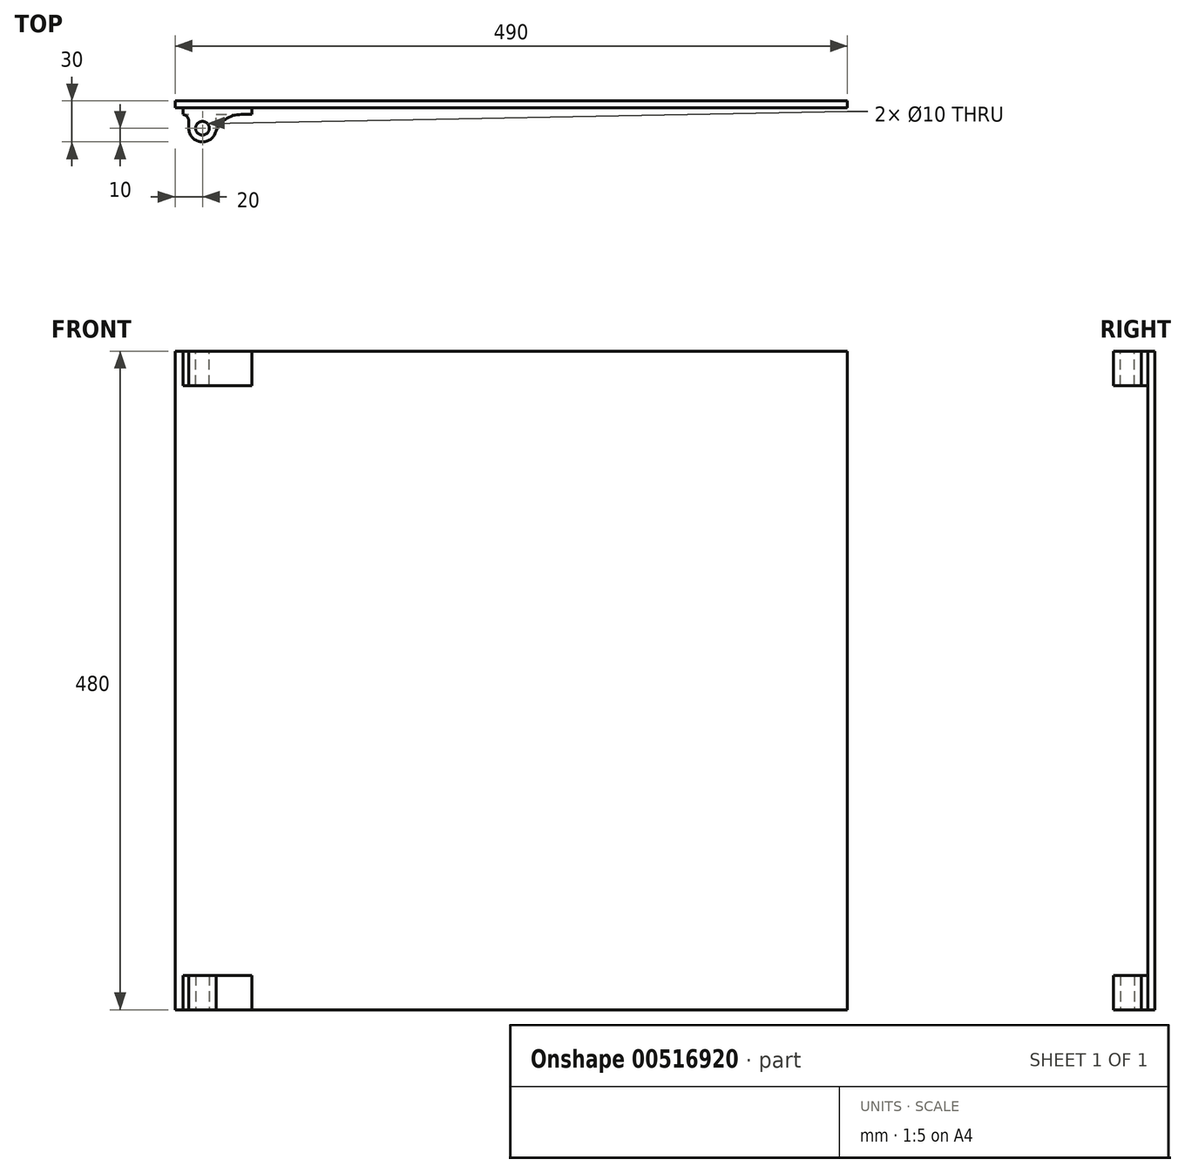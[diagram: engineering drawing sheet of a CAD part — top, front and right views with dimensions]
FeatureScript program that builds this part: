
annotation { "Feature Type Name" : "Feature", "Feature Type Description" : "" }
export const myFeature = defineFeature(function(context is Context, id is Id, definition is map)
    precondition{}
    {
        {
            var Q0;
            Q0=qCreatedBy(makeId("Front.planeOp"),FACE);
            var sketch = newSketch(context, id + "F0", { "sketchPlane" : qUnion([Q0])});
            skLineSegment(sketch, "E0.bottom", {"start": v(245, 240) * mm, "end": v(-245, 240) * mm});
            skLineSegment(sketch, "E0.top", {"start": v(245, -240) * mm, "end": v(-245, -240) * mm});
            skLineSegment(sketch, "E0.left", {"start": v(245, 240) * mm, "end": v(245, -240) * mm});
            skLineSegment(sketch, "E0.right", {"start": v(-245, 240) * mm, "end": v(-245, -240) * mm});
            skPoint(sketch, "E0.middle", {"position": v(0, 0) * mm});
            skSolve(sketch);
        }
        {
            var Q0;
            Q0=makeQuery(id+"F0.imprint","IMPRINT",FACE,{"disambiguationData":[TD([[makeQuery(id+"F0.imprint","IMPRINT",EDGE,{"derivedFrom":sQuery(id+"F0.wireOp",EDGE,"E0.bottom")}),1.0]])]});
            extrude(context, id + "F1", {"entities" : qUnion([Q0]), "depth" : 5 * mm, "offsetDistance" : 25 * mm});
        }
        {
            var Q0;
            Q0=makeQuery(id+"F1.opExtrude","SWEPT_FACE",FACE,{"disambiguationData":[OSD([sQuery(id+"F0.wireOp",EDGE,"E0.bottom")])]});
            var sketch = newSketch(context, id + "F2", { "sketchPlane" : qUnion([Q0])});
            skLineSegment(sketch, "E1.0", {"start": v(245, -5) * mm, "end": v(-245, -5) * mm});
            skLineSegment(sketch, "E2", {"start": v(-239, -5) * mm, "end": v(-239, -10) * mm});
            skLineSegment(sketch, "E3", {"start": v(-239, -10) * mm, "end": v(-189, -10) * mm});
            skLineSegment(sketch, "E4", {"start": v(-189, -10) * mm, "end": v(-189, -5) * mm});
            skLineSegment(sketch, "E5", {"start": v(-189, -5) * mm, "end": v(-239, -5) * mm});
            skCircle(sketch, "E6", {"center": v(-225, -20) * mm, "radius": 10 * mm});
            skCircle(sketch, "E7", {"center": v(-225, -20) * mm, "radius": 5 * mm});
            skLineSegment(sketch, "E8", {"start": v(-235, -20) * mm, "end": v(-235, -10) * mm});
            skLineSegment(sketch, "E9", {"start": v(-215, -20) * mm, "end": v(-215, -10) * mm});
            skSolve(sketch);
        }
        {
            var Q0;
            {var subQ4=sQuery(id+"F2.wireOp",EDGE,"E2");Q0=makeQuery(id+"F2.imprint","IMPRINT",FACE,{"disambiguationData":[TD([[makeQuery(id+"F2.imprint","IMPRINT",EDGE,{"derivedFrom":subQ4}),1.0]])]});}
            var Q1;
            Q1=makeQuery(id+"F2.imprint","IMPRINT",FACE,{"disambiguationData":[TD([[makeQuery(id+"F2.imprint","IMPRINT",EDGE,{"derivedFrom":sQuery(id+"F2.wireOp",EDGE,"E7")}),-1.0]])]});
            var Q2;
            {var subQ0=sQuery(id+"F2.wireOp",EDGE,"E9");Q2=makeQuery(id+"F2.imprint","IMPRINT",FACE,{"disambiguationData":[TD([[makeQuery(id+"F2.imprint","IMPRINT",EDGE,{"derivedFrom":subQ0}),1.0]])]});}
            var Q3;
            {var subQ0=sQuery(id+"F2.wireOp",EDGE,"E8");Q3=makeQuery(id+"F2.imprint","IMPRINT",FACE,{"disambiguationData":[TD([[makeQuery(id+"F2.imprint","IMPRINT",EDGE,{"derivedFrom":subQ0}),-1.0]])]});}
            extrude(context, id + "F3", {"entities" : qUnion([Q0, Q1, Q2, Q3]), "oppositeDirection" : true, "depth" : 25 * mm, "offsetDistance" : 25 * mm});
        }
        {
            var Q0;
            Q0=makeQuery(id+"F3.opExtrude","SWEPT_BODY",BODY,{"disambiguationData":[OSD([sQuery(id+"F2.wireOp",EDGE,"E2"),sQuery(id+"F2.wireOp",EDGE,"E3"),sQuery(id+"F2.wireOp",EDGE,"E4"),sQuery(id+"F2.wireOp",EDGE,"E5"),sQuery(id+"F2.wireOp",EDGE,"E6"),sQuery(id+"F2.wireOp",EDGE,"E7"),sQuery(id+"F2.wireOp",EDGE,"E8"),sQuery(id+"F2.wireOp",EDGE,"E9")])]});
            var Q1;
            Q1=qCreatedBy(makeId("Top.planeOp"),FACE);
            mirror(context, id + "F4", {"entities" : qUnion([Q0]), "mirrorPlane" : qUnion([Q1])});
        }
        {
            var Q0;
            Q0=makeQuery(id+"F1.opExtrude","CAP_FACE",FACE,{"disambiguationData":[OSD([sQuery(id+"F0.wireOp",EDGE,"E0.bottom"),sQuery(id+"F0.wireOp",EDGE,"E0.top"),sQuery(id+"F0.wireOp",EDGE,"E0.left"),sQuery(id+"F0.wireOp",EDGE,"E0.right")])],"isStart":false});
            var sketch = newSketch(context, id + "F5", { "sketchPlane" : qUnion([Q0])});
            skLineSegment(sketch, "E10", {"start": v(-239, -240) * mm, "end": v(-239, 240) * mm, "construction": true});
            skSolve(sketch);
        }
        {
            var Q0;
            Q0=makeQuery(id+"F3.opExtrude","SWEPT_EDGE",EDGE,{"disambiguationData":[OSD([sQuery(id+"F2.wireOp",EDGE,"E3"),sQuery(id+"F2.wireOp",EDGE,"E9")])]});
            fillet(context, id + "F6", {"entities" : qUnion([Q0]), "radius" : 20 * mm, "tangentPropagation" : true, "allowEdgeOverflow" : false});
        }
        {
            var Q0;
            Q0=makeQuery(id+"F3.opExtrude","SWEPT_EDGE",EDGE,{"disambiguationData":[OSD([sQuery(id+"F2.wireOp",EDGE,"E3"),sQuery(id+"F2.wireOp",EDGE,"E8")])]});
            fillet(context, id + "F7", {"entities" : qUnion([Q0]), "radius" : 5 * mm, "tangentPropagation" : true, "allowEdgeOverflow" : false});
        }
    });
